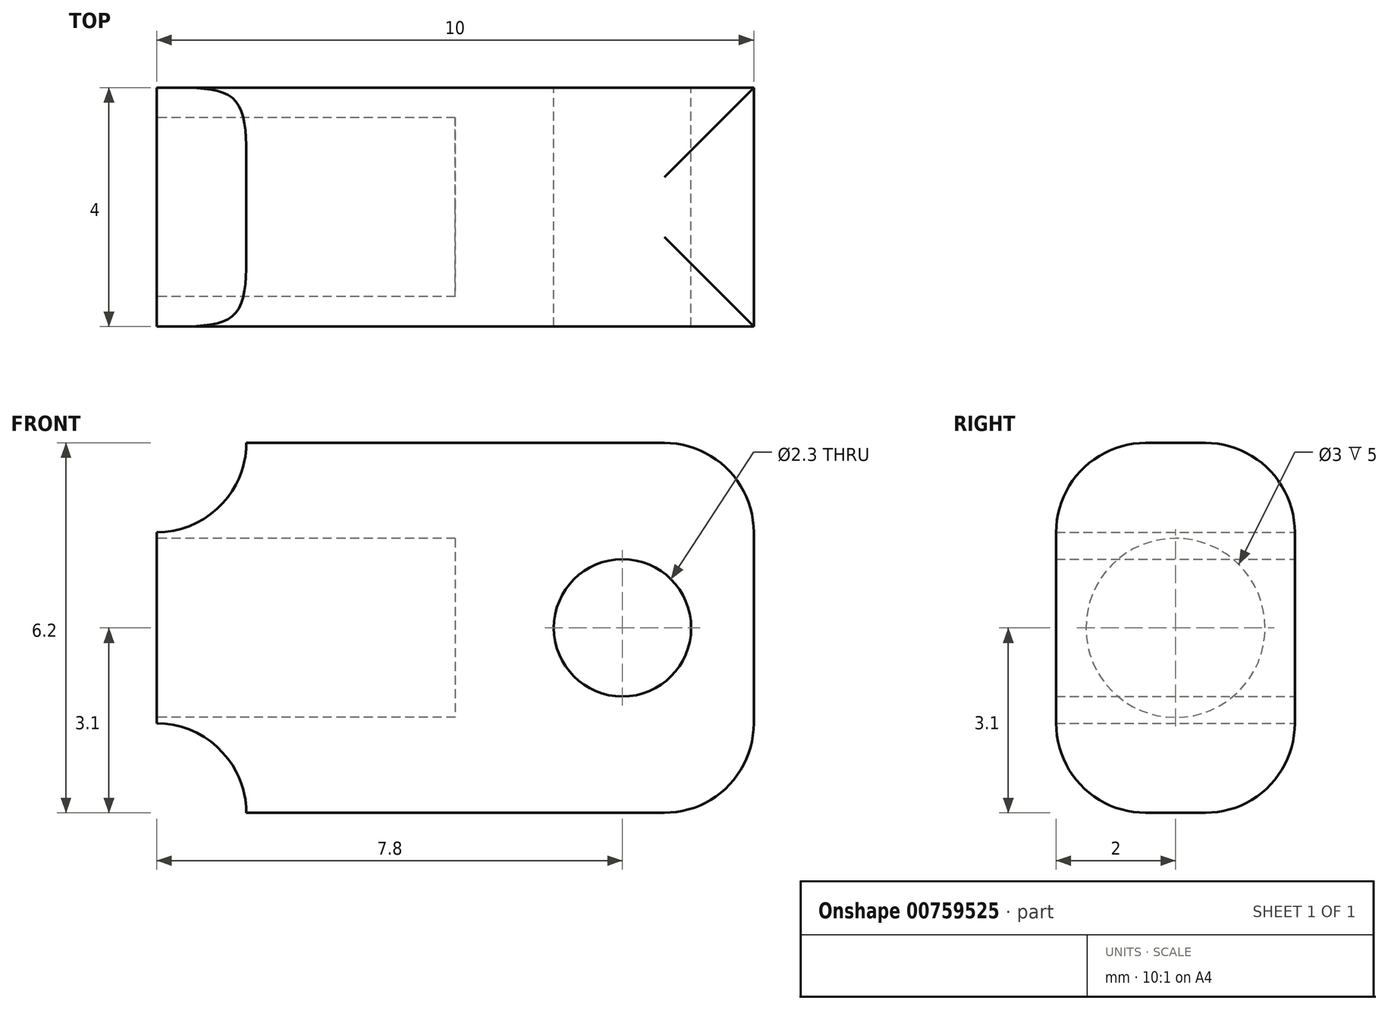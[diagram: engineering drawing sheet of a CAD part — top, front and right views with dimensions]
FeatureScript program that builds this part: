
annotation { "Feature Type Name" : "Feature", "Feature Type Description" : "" }
export const myFeature = defineFeature(function(context is Context, id is Id, definition is map)
    precondition{}
    {
        {
            var Q0;
            Q0=qCreatedBy(makeId("Front.planeOp"),FACE);
            var sketch = newSketch(context, id + "F0", { "sketchPlane" : qUnion([Q0])});
            skLineSegment(sketch, "E0.bottom", {"start": v(5, 3.1) * mm, "end": v(-3.5, 3.1) * mm});
            skLineSegment(sketch, "E0.top", {"start": v(5, -3.1) * mm, "end": v(-3.5, -3.1) * mm});
            skLineSegment(sketch, "E0.left", {"start": v(5, 3.1) * mm, "end": v(5, -3.1) * mm});
            skLineSegment(sketch, "E0.right", {"start": v(-5, 1.6) * mm, "end": v(-5, -1.6) * mm});
            skPoint(sketch, "E0.middle", {"position": v(0, 0) * mm});
            skArc(sketch, "E1", {"start": v(-5, 1.6) * mm, "mid": v(-3.94, 2.04) * mm, "end": v(-3.5, 3.1) * mm});
            skArc(sketch, "E2", {"start": v(-3.5, -3.1) * mm, "mid": v(-3.94, -2.04) * mm, "end": v(-5, -1.6) * mm});
            skCircle(sketch, "E3", {"center": v(2.8, 0) * mm, "radius": 1.15 * mm});
            skSolve(sketch);
        }
        {
            var Q0;
            Q0 = qSketchRegion(id + "F0", true);
            extrude(context, id + "F1", {"entities" : qUnion([Q0]), "depth" : 4 * mm, "offsetDistance" : 25 * mm});
        }
        {
            var Q0;
            Q0=makeQuery(id+"F1.opExtrude","SWEPT_FACE",FACE,{"disambiguationData":[OSD([sQuery(id+"F0.wireOp",EDGE,"E0.right")])]});
            var sketch = newSketch(context, id + "F2", { "sketchPlane" : qUnion([Q0])});
            skCircle(sketch, "E4", {"center": v(2, 0) * mm, "radius": 1.5 * mm});
            skSolve(sketch);
        }
        {
            var Q0;
            Q0 = qSketchRegion(id + "F2", true);
            extrude(context, id + "F3", {"entities" : qUnion([Q0]), "operationType" : NewBodyOperationType.REMOVE, "oppositeDirection" : true, "depth" : 5 * mm, "offsetDistance" : 25 * mm});
        }
        {
            var Q0;
            Q0=makeQuery(id+"F1.opExtrude","SWEPT_EDGE",EDGE,{"disambiguationData":[OSD([sQuery(id+"F0.wireOp",EDGE,"E0.bottom"),sQuery(id+"F0.wireOp",EDGE,"E0.left")])]});
            var Q1;
            Q1=makeQuery(id+"F1.opExtrude","SWEPT_EDGE",EDGE,{"disambiguationData":[OSD([sQuery(id+"F0.wireOp",EDGE,"E0.top"),sQuery(id+"F0.wireOp",EDGE,"E0.left")])]});
            var Q2;
            Q2=makeQuery(id+"F1.opExtrude","CAP_EDGE",EDGE,{"disambiguationData":[OSD([sQuery(id+"F0.wireOp",EDGE,"E0.bottom")])],"isStart":false});
            var Q3;
            Q3=makeQuery(id+"F1.opExtrude","CAP_EDGE",EDGE,{"disambiguationData":[OSD([sQuery(id+"F0.wireOp",EDGE,"E0.bottom")])],"isStart":true});
            var Q4;
            Q4=makeQuery(id+"F1.opExtrude","CAP_EDGE",EDGE,{"disambiguationData":[OSD([sQuery(id+"F0.wireOp",EDGE,"E0.top")])],"isStart":false});
            var Q5;
            Q5=makeQuery(id+"F1.opExtrude","CAP_EDGE",EDGE,{"disambiguationData":[OSD([sQuery(id+"F0.wireOp",EDGE,"E0.top")])],"isStart":true});
            fillet(context, id + "F4", {"entities" : qUnion([Q0, Q1, Q2, Q3, Q4, Q5]), "radius" : 1.5 * mm, "tangentPropagation" : true, "allowEdgeOverflow" : false});
        }
    });
